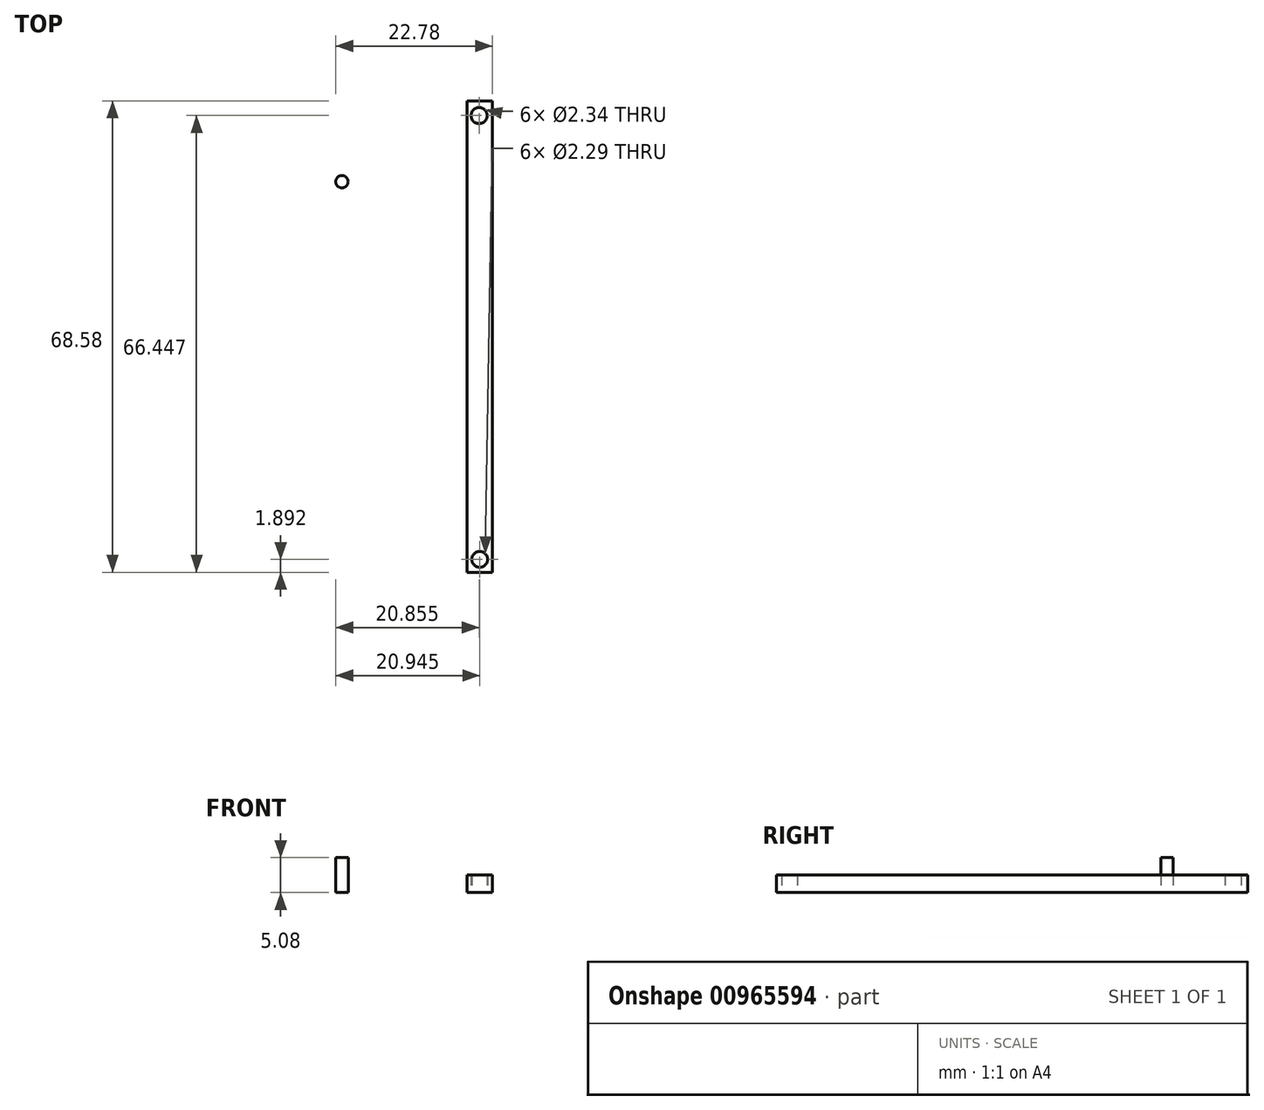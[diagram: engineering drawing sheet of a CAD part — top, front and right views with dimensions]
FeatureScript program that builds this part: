
annotation { "Feature Type Name" : "Feature", "Feature Type Description" : "" }
export const myFeature = defineFeature(function(context is Context, id is Id, definition is map)
    precondition{}
    {
        {
            var Q0;
            Q0=qCreatedBy(makeId("Top.planeOp"),FACE);
            var sketch = newSketch(context, id + "F0", { "sketchPlane" : qUnion([Q0])});
            skLineSegment(sketch, "E0.bottom", {"start": v(-40.85, 37.67) * mm, "end": v(-37.18, 37.67) * mm});
            skLineSegment(sketch, "E0.top", {"start": v(-40.85, -30.9) * mm, "end": v(-37.18, -30.9) * mm});
            skLineSegment(sketch, "E0.left", {"start": v(-40.85, 37.67) * mm, "end": v(-40.85, -30.9) * mm});
            skLineSegment(sketch, "E0.right", {"start": v(-37.18, 37.67) * mm, "end": v(-37.18, -30.9) * mm});
            skCircle(sketch, "E1", {"center": v(-39.1, 35.54) * mm, "radius": 1.17 * mm});
            skCircle(sketch, "E2", {"center": v(-39.02, -29.02) * mm, "radius": 1.14 * mm});
            skPoint(sketch, "E2.centerSnap0", {"position": v(-39.02, -30.9) * mm});
            skCircle(sketch, "E3", {"center": v(-59.06, 25.91) * mm, "radius": 0.9 * mm});
            skSolve(sketch);
        }
        {
            var Q0;
            Q0=makeQuery(id+"F0.imprint","IMPRINT",FACE,{"disambiguationData":[TD([[makeQuery(id+"F0.imprint","IMPRINT",EDGE,{"derivedFrom":sQuery(id+"F0.wireOp",EDGE,"E0.bottom")}),-1.0]])]});
            extrude(context, id + "F1", {"entities" : qUnion([Q0]), "depth" : 2.54 * mm, "offsetDistance" : 25.4 * mm});
        }
        {
            var Q0;
            Q0=makeQuery(id+"F0.imprint","IMPRINT",FACE,{"disambiguationData":[TD([[makeQuery(id+"F0.imprint","IMPRINT",EDGE,{"derivedFrom":sQuery(id+"F0.wireOp",EDGE,"E3")}),1.0]])]});
            extrude(context, id + "F2", {"entities" : qUnion([Q0]), "depth" : 5.08 * mm, "offsetDistance" : 25.4 * mm});
        }
    });
